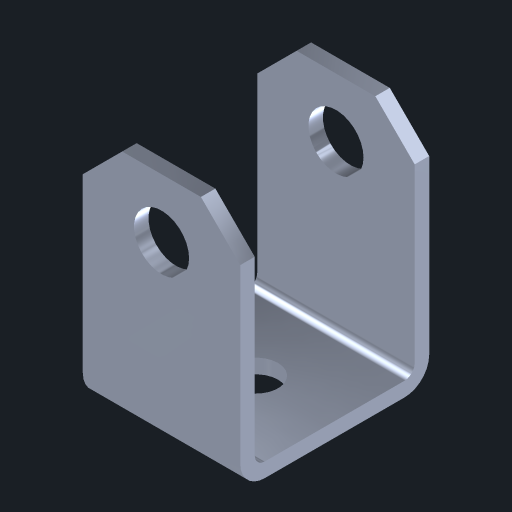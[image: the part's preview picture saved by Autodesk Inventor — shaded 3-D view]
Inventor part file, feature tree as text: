
AUTODESK INVENTOR PART (.ipt)
format: ipt  version: 2023 (Build 270158030, 158C)  size: 157,696 bytes
history: native  units: in
note: dims shown in document units (in); Inventor stores cm internally (conversion verified against a paired STEP export)
features: chamfer x1, other x1, imported_body x1
ambient origin geometry x8: Origin, YZ Plane, XZ Plane, XY Plane, X Axis, Y Axis, Z Axis, Center Point
bodies: Body1 (feature_tree)
feature tree (3):
  chamfer  "Chamfer1"  [1 undecoded]
  other  "VL-PNEU-BRK-0011"
  imported_body  "Base1"
note: 1 required parameter value undecoded (feature->parameter linkage not recoverable at this tier; creation-order binding heuristic only, values carry confidence <= 0.55)
